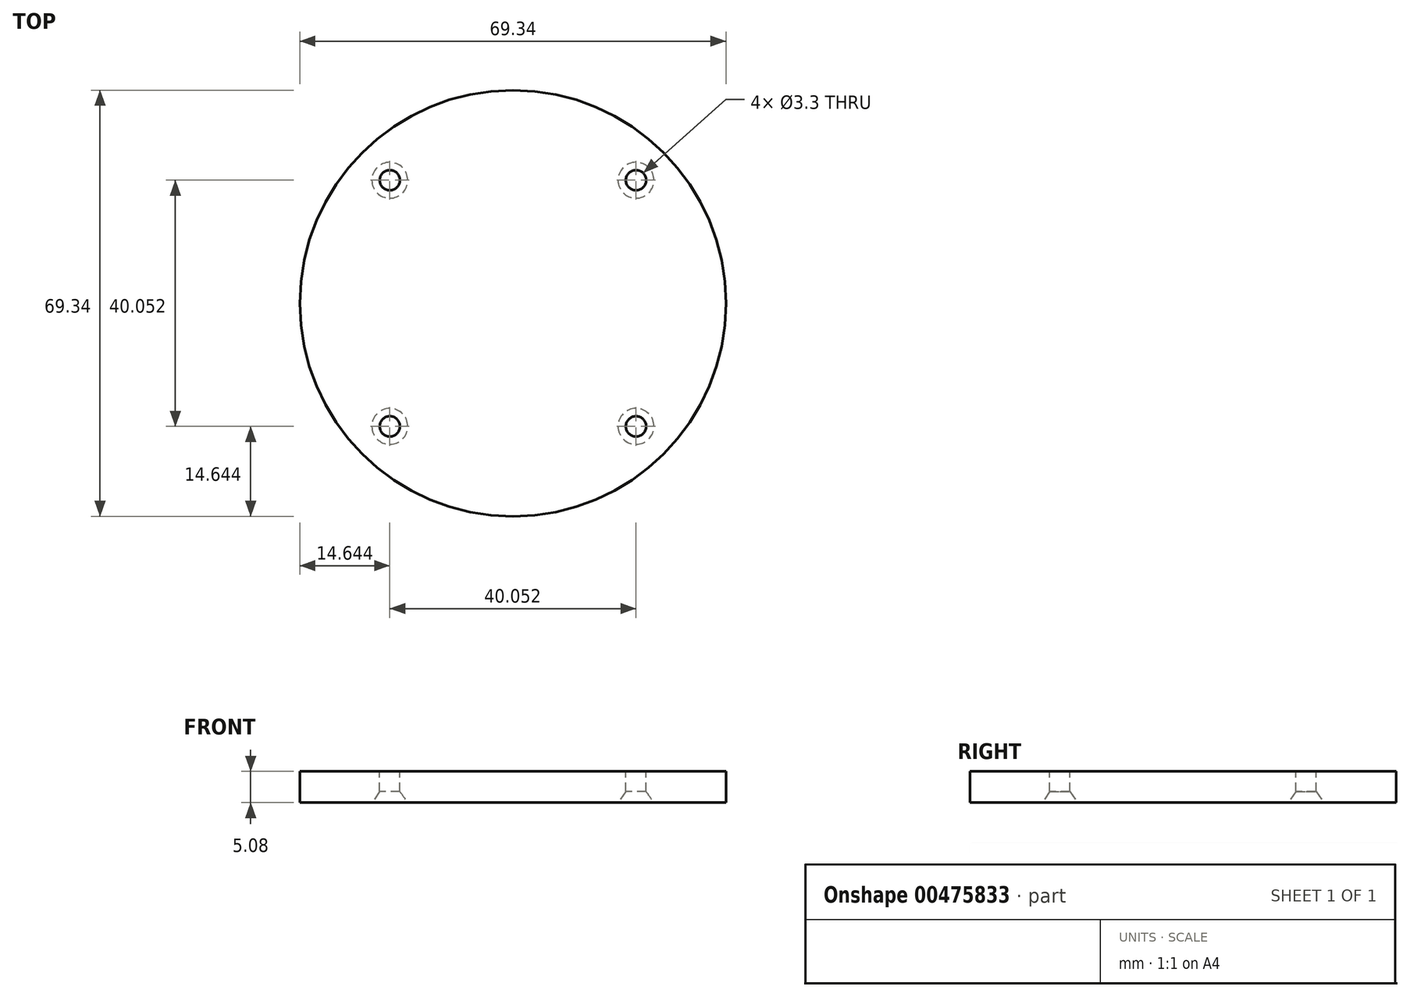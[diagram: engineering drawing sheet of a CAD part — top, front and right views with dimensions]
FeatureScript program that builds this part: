
annotation { "Feature Type Name" : "Feature", "Feature Type Description" : "" }
export const myFeature = defineFeature(function(context is Context, id is Id, definition is map)
    precondition{}
    {
        {
            var Q0;
            Q0=qCreatedBy(makeId("Top.planeOp"),FACE);
            var sketch = newSketch(context, id + "F0", { "sketchPlane" : qUnion([Q0])});
            skCircle(sketch, "E0", {"center": v(0, 0) * mm, "radius": 34.67 * mm});
            skSolve(sketch);
        }
        {
            var Q0;
            Q0=qSketchRegion(id+"F0",true);
            extrude(context, id + "F1", {"entities" : qUnion([Q0]), "depth" : 5.08 * mm});
        }
        {
            var Q0;
            Q0=makeQuery(id+"F1.opExtrude","CAP_FACE",FACE,{"disambiguationData":[OSD([sQuery(id+"F0.wireOp",EDGE,"E0")])],"isStart":false});
            var sketch = newSketch(context, id + "F2", { "sketchPlane" : qUnion([Q0])});
            skLineSegment(sketch, "E1", {"start": v(0, 0) * mm, "end": v(24.52, 24.52) * mm});
            skLineSegment(sketch, "E2", {"start": v(24.52, 24.52) * mm, "end": v(-24.52, -24.52) * mm});
            skLineSegment(sketch, "E3", {"start": v(-24.52, 24.52) * mm, "end": v(24.52, -24.52) * mm});
            skCircle(sketch, "E4", {"center": v(20.03, 20.03) * mm, "radius": 1.65 * mm});
            skCircle(sketch, "E5.1.0", {"center": v(-20.03, 20.03) * mm, "radius": 1.65 * mm});
            skCircle(sketch, "E5.2.0", {"center": v(-20.03, -20.03) * mm, "radius": 1.65 * mm});
            skCircle(sketch, "E5.3.0", {"center": v(20.03, -20.03) * mm, "radius": 1.65 * mm});
            skPoint(sketch, "E5.center", {"position": v(0, 0) * mm});
            skSolve(sketch);
        }
        {
            var Q0;
            Q0=qSketchRegion(id+"F2",true);
            extrude(context, id + "F3", {"entities" : qUnion([Q0]), "operationType" : NewBodyOperationType.REMOVE, "oppositeDirection" : true, "depth" : 25.4 * mm});
        }
        {
            var Q0;
            Q0=makeQuery(id+"F3.boolean.opBoolean","INTERSECT",EDGE,{"derivedFrom":[makeQuery(id+"F1.opExtrude","CAP_FACE",FACE,{"disambiguationData":[OSD([sQuery(id+"F0.wireOp",EDGE,"E0")])],"isStart":true}),makeQuery(id+"F3.opExtrude","SWEPT_FACE",FACE,{"disambiguationData":[OSD([sQuery(id+"F2.wireOp",EDGE,"E5.2.0")])]})]});
            var Q1;
            Q1=makeQuery(id+"F3.boolean.opBoolean","INTERSECT",EDGE,{"derivedFrom":[makeQuery(id+"F1.opExtrude","CAP_FACE",FACE,{"disambiguationData":[OSD([sQuery(id+"F0.wireOp",EDGE,"E0")])],"isStart":true}),makeQuery(id+"F3.opExtrude","SWEPT_FACE",FACE,{"disambiguationData":[OSD([sQuery(id+"F2.wireOp",EDGE,"E5.3.0")])]})]});
            var Q2;
            Q2=makeQuery(id+"F3.boolean.opBoolean","INTERSECT",EDGE,{"derivedFrom":[makeQuery(id+"F1.opExtrude","CAP_FACE",FACE,{"disambiguationData":[OSD([sQuery(id+"F0.wireOp",EDGE,"E0")])],"isStart":true}),makeQuery(id+"F3.opExtrude","SWEPT_FACE",FACE,{"disambiguationData":[OSD([sQuery(id+"F2.wireOp",EDGE,"E4")])]})]});
            var Q3;
            Q3=makeQuery(id+"F3.boolean.opBoolean","INTERSECT",EDGE,{"derivedFrom":[makeQuery(id+"F1.opExtrude","CAP_FACE",FACE,{"disambiguationData":[OSD([sQuery(id+"F0.wireOp",EDGE,"E0")])],"isStart":true}),makeQuery(id+"F3.opExtrude","SWEPT_FACE",FACE,{"disambiguationData":[OSD([sQuery(id+"F2.wireOp",EDGE,"E5.1.0")])]})]});
            chamfer(context, id + "F4", {"entities" : qUnion([Q0, Q1, Q2, Q3]), "chamferType" : ChamferType.TWO_OFFSETS, "width1" : 1.27 * mm, "oppositeDirection" : false, "width2" : 1.78 * mm, "tangentPropagation" : true});
        }
    });
